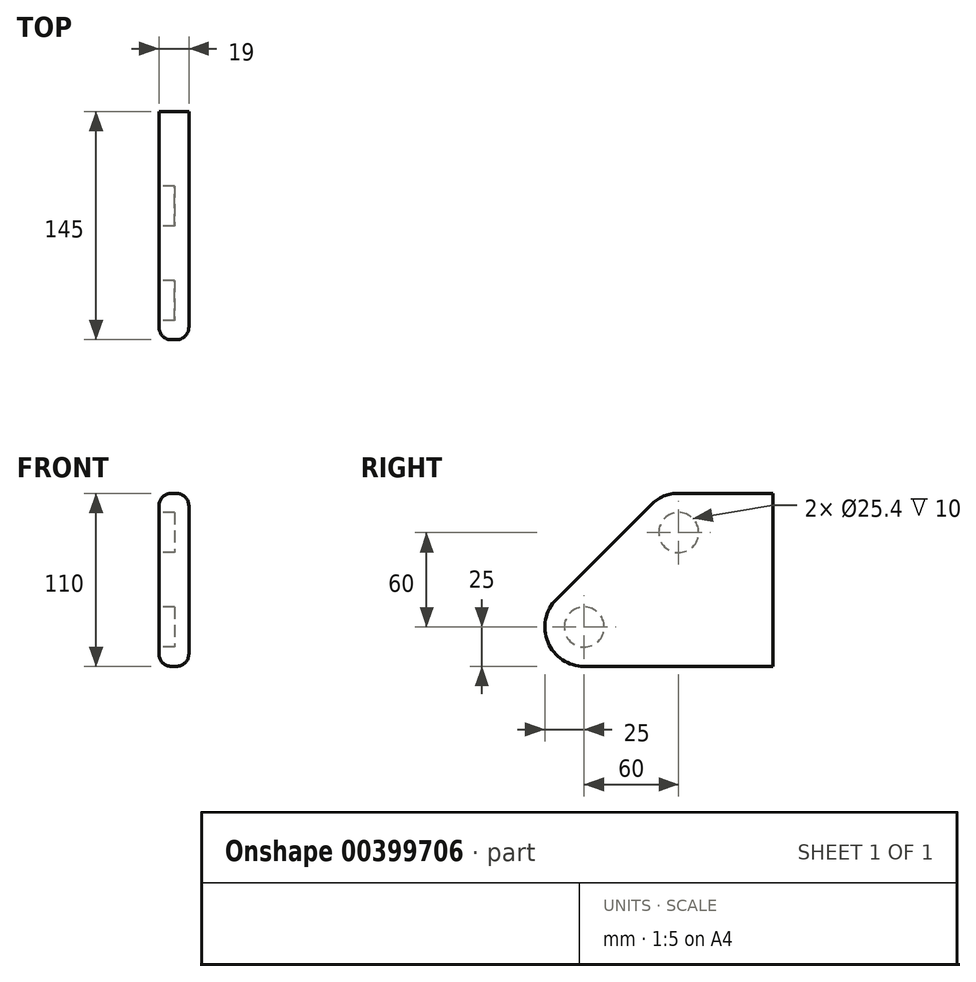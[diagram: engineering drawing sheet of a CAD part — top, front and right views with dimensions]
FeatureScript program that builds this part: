
annotation { "Feature Type Name" : "Feature", "Feature Type Description" : "" }
export const myFeature = defineFeature(function(context is Context, id is Id, definition is map)
    precondition{}
    {
        {
            var Q0;
            Q0=qCreatedBy(makeId("Right.planeOp"),FACE);
            var sketch = newSketch(context, id + "F0", { "sketchPlane" : qUnion([Q0])});
            skLineSegment(sketch, "E0", {"start": v(0, 0) * mm, "end": v(-120, 0) * mm});
            skLineSegment(sketch, "E1", {"start": v(-145, 0) * mm, "end": v(-120, 0) * mm, "construction": true});
            skLineSegment(sketch, "E2", {"start": v(-120, 0) * mm, "end": v(-120, 25) * mm, "construction": true});
            skLineSegment(sketch, "E3", {"start": v(-120, 25) * mm, "end": v(-39.37, 25) * mm, "construction": true});
            skLineSegment(sketch, "E4", {"start": v(-120, 25) * mm, "end": v(-19.56, 125.44) * mm, "construction": true});
            skLineSegment(sketch, "E5", {"start": v(-120, 25) * mm, "end": v(0, 25) * mm, "construction": true});
            skPoint(sketch, "E5.endSnap0", {"position": v(-79.68, 25) * mm});
            skLineSegment(sketch, "E6", {"start": v(-60, 25) * mm, "end": v(-60, 85) * mm, "construction": true});
            skLineSegment(sketch, "E7", {"start": v(-60, 85) * mm, "end": v(-60, 110) * mm, "construction": true});
            skLineSegment(sketch, "E8", {"start": v(0, 110) * mm, "end": v(0, 0) * mm});
            skLineSegment(sketch, "E9", {"start": v(-60, 85) * mm, "end": v(-77.68, 102.68) * mm, "construction": true});
            skLineSegment(sketch, "E10", {"start": v(-120, 25) * mm, "end": v(-137.68, 42.68) * mm, "construction": true});
            skPoint(sketch, "E11.newPointB", {"position": v(-145, 0) * mm});
            skArc(sketch, "E11.filletArc", {"start": v(-137.68, 42.68) * mm, "mid": v(-143.1, 15.43) * mm, "end": v(-120, 0) * mm});
            skLineSegment(sketch, "E12", {"start": v(-137.68, 42.68) * mm, "end": v(-77.68, 102.68) * mm});
            skLineSegment(sketch, "E13", {"start": v(-60, 110) * mm, "end": v(0, 110) * mm});
            skArc(sketch, "E14.filletArc", {"start": v(-60, 110) * mm, "mid": v(-69.57, 108.1) * mm, "end": v(-77.68, 102.68) * mm});
            skSolve(sketch);
        }
        {
            var Q0;
            Q0 = qSketchRegion(id + "F0", true);
            extrude(context, id + "F1", {"entities" : qUnion([Q0]), "depth" : 19 * mm});
        }
        {
            var Q0;
            Q0=makeQuery(id+"F1.opExtrude","CAP_FACE",FACE,{"disambiguationData":[OSD([sQuery(id+"F0.wireOp",EDGE,"E0"),sQuery(id+"F0.wireOp",EDGE,"E8"),sQuery(id+"F0.wireOp",EDGE,"E11.filletArc"),sQuery(id+"F0.wireOp",EDGE,"E12"),sQuery(id+"F0.wireOp",EDGE,"E13"),sQuery(id+"F0.wireOp",EDGE,"E14.filletArc")])],"isStart":true});
            var sketch = newSketch(context, id + "F2", { "sketchPlane" : qUnion([Q0])});
            skCircle(sketch, "E15", {"center": v(60, 85) * mm, "radius": 12.7 * mm});
            skCircle(sketch, "E16", {"center": v(120, 25) * mm, "radius": 12.7 * mm});
            skSolve(sketch);
        }
        {
            var Q0;
            Q0 = qSketchRegion(id + "F2", true);
            extrude(context, id + "F3", {"entities" : qUnion([Q0]), "operationType" : NewBodyOperationType.REMOVE, "oppositeDirection" : true, "depth" : 10 * mm});
        }
        {
            var Q0;
            Q0=makeQuery(id+"F1.opExtrude","CAP_EDGE",EDGE,{"disambiguationData":[OSD([sQuery(id+"F0.wireOp",EDGE,"E13")])],"isStart":true});
            fillet(context, id + "F4", {"entities" : qUnion([Q0]), "radius" : 8 * mm, "tangentPropagation" : true, "allowEdgeOverflow" : false});
        }
        {
            var Q0;
            Q0=makeQuery(id+"F1.opExtrude","CAP_EDGE",EDGE,{"disambiguationData":[OSD([sQuery(id+"F0.wireOp",EDGE,"E13")])],"isStart":false});
            fillet(context, id + "F5", {"entities" : qUnion([Q0]), "radius" : 8 * mm, "tangentPropagation" : true, "allowEdgeOverflow" : false});
        }
    });
